# Revit family: 203_DAOSL-_
name_source: partatom
category: Duct Accessories
units: mm (PartAtom-declared; Revit-internal decimal feet)

## family parameters
Always vertical = Yes
Cut with Voids When Loaded = No
Part Type = Damper
Round Connector Dimension = Use Diameter
Shared = No
Work Plane-Based = No

## types (11) — shared parameters
CAT0 = Yes
Description = RETURN DAMPER WITH GASKET
Manufacturer = Alnor
QmdConnectorList = 201;D;202;D
URL = http://www.ventilation-alnor.co.uk
magiPartTypeId = 203
magiProductFamilyId = DAOSL-*

## per-type parameters (varying)
| type | D | H2D | L | L2D | LL | R | W2D |
| DAOSL-80 | 80 mm | 80 mm  [stored 0.262467 ft] | 92 mm  [stored 0.301837 ft] | 92 mm  [stored 0.301837 ft] | 46 mm  [stored 0.150919 ft] | 40 mm  [stored 0.131234 ft] | 80 mm  [stored 0.262467 ft] |
| DAOSL-450 | 450 mm | 450 mm | 170 mm | 170 mm | 85 mm | 225 mm | 450 mm |
| DAOSL-400 | 400 mm | 400 mm | 126 mm | 126 mm | 63 mm | 200 mm | 400 mm |
| DAOSL-355 | 355 mm | 355 mm | 126 mm | 126 mm | 63 mm | 178 mm | 355 mm |
| DAOSL-315 | 315 mm | 315 mm | 92 mm  [stored 0.301837 ft] | 135 mm | 46 mm  [stored 0.150919 ft] | 158 mm | 315 mm |
| DAOSL-250 | 250 mm | 250 mm | 92 mm  [stored 0.301837 ft] | 135 mm | 46 mm  [stored 0.150919 ft] | 125 mm | 250 mm |
| DAOSL-200 | 200 mm | 200 mm | 92 mm  [stored 0.301837 ft] | 92 mm  [stored 0.301837 ft] | 46 mm  [stored 0.150919 ft] | 100 mm  [stored 0.328084 ft] | 200 mm |
| DAOSL-160 | 160 mm | 160 mm | 92 mm  [stored 0.301837 ft] | 92 mm  [stored 0.301837 ft] | 46 mm  [stored 0.150919 ft] | 80 mm  [stored 0.262467 ft] | 160 mm |
| DAOSL-150 | 150 mm | 150 mm | 92 mm  [stored 0.301837 ft] | 210 mm | 46 mm  [stored 0.150919 ft] | 75 mm | 150 mm |
| DAOSL-125 | 125 mm | 125 mm | 92 mm  [stored 0.301837 ft] | 92 mm  [stored 0.301837 ft] | 46 mm  [stored 0.150919 ft] | 63 mm | 125 mm |
| DAOSL-100 | 100 mm | 100 mm  [stored 0.328084 ft] | 92 mm  [stored 0.301837 ft] | 92 mm  [stored 0.301837 ft] | 46 mm  [stored 0.150919 ft] | 50 mm | 100 mm  [stored 0.328084 ft] |

note: column(s) folded — value = type name in every type: MC Product Code, magiProductId

note: [stored X ft] marks values corroborated as IEEE doubles in the binary element streams (Revit-internal decimal feet)

## geometry (parser evidence)
native form markers: Blend x4, Sweep x2
no freeform markers — native parametric forms only
